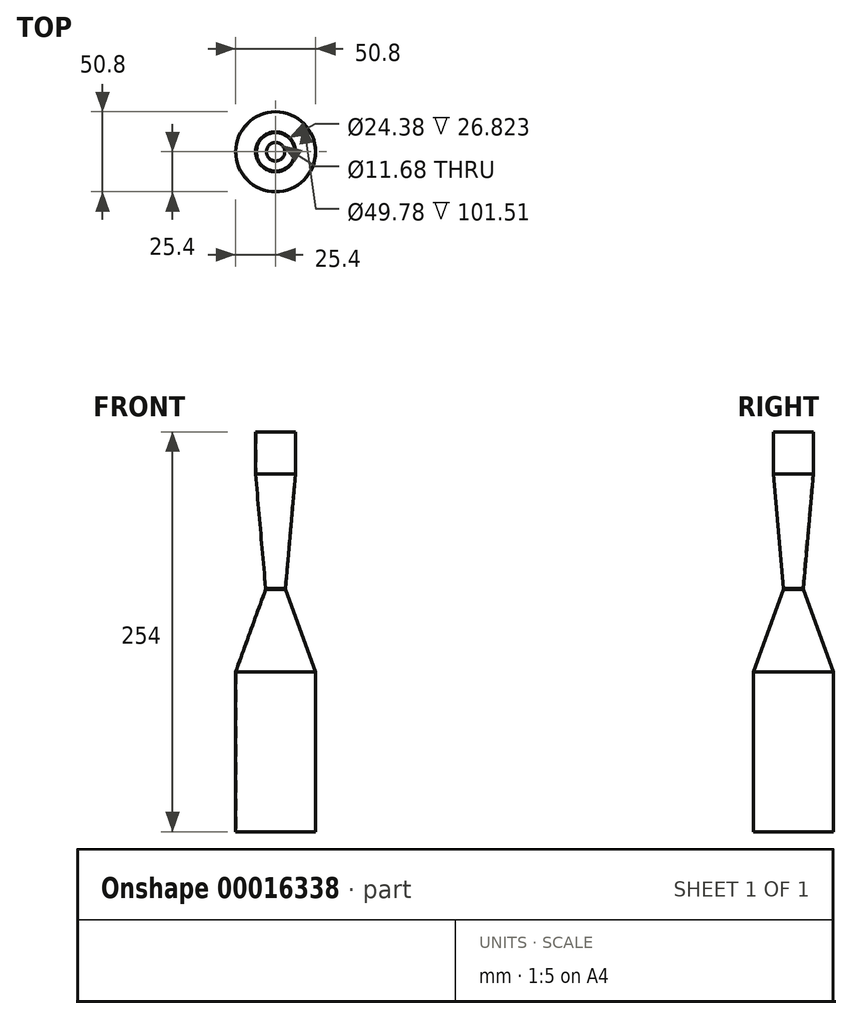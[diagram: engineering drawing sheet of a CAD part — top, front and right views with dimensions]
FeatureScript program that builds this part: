
annotation { "Feature Type Name" : "Feature", "Feature Type Description" : "" }
export const myFeature = defineFeature(function(context is Context, id is Id, definition is map)
    precondition{}
    {
        {
            var Q0;
            Q0=qCreatedBy(makeId("Front.planeOp"),FACE);
            var sketch = newSketch(context, id + "F0", { "sketchPlane" : qUnion([Q0])});
            skLineSegment(sketch, "E0", {"start": v(0, 0) * mm, "end": v(0, 99.43) * mm});
            skLineSegment(sketch, "E1", {"start": v(0, 99.43) * mm, "end": v(-12.7, 99.43) * mm});
            skLineSegment(sketch, "E2", {"start": v(-12.7, 99.43) * mm, "end": v(-12.7, 72.58) * mm});
            skLineSegment(sketch, "E3", {"start": v(-12.7, 72.58) * mm, "end": v(-6.35, 0) * mm});
            skLineSegment(sketch, "E4", {"start": v(-6.35, 0) * mm, "end": v(-6.35, -0.64) * mm});
            skLineSegment(sketch, "E5", {"start": v(-6.35, -0.63) * mm, "end": v(-25.4, -52.97) * mm});
            skLineSegment(sketch, "E6", {"start": v(-25.4, -52.97) * mm, "end": v(-25.4, -154.57) * mm});
            skLineSegment(sketch, "E7", {"start": v(-25.4, -154.57) * mm, "end": v(0, -154.57) * mm});
            skLineSegment(sketch, "E8", {"start": v(-6.35, 0) * mm, "end": v(0, 0) * mm, "construction": true});
            skLineSegment(sketch, "E9", {"start": v(0, 0) * mm, "end": v(0, -154.57) * mm});
            skSolve(sketch);
        }
        {
            var Q0;
            Q0=makeQuery(id+"F0.imprint","IMPRINT",FACE,{"disambiguationData":[TD([[makeQuery(id+"F0.imprint","IMPRINT",EDGE,{"derivedFrom":sQuery(id+"F0.wireOp",EDGE,"E0")}),1.0]])]});
            var Q1;
            Q1=sQuery(id+"F0.wireOp",EDGE,"E0");
            revolve(context, id + "F1", {"entities" : qUnion([Q0]), "axis" : qUnion([Q1]), "revolveType" : RevolveType.FULL});
        }
        {
            var Q0;
            Q0=makeQuery(id+"F1.opRevolve","SWEPT_FACE",FACE,{"disambiguationData":[OSD([sQuery(id+"F0.wireOp",EDGE,"E7")])]});
            var Q1;
            Q1=makeQuery(id+"F1.opRevolve","SWEPT_FACE",FACE,{"disambiguationData":[OSD([sQuery(id+"F0.wireOp",EDGE,"E1")])]});
            shell(context, id + "F2", {"entities" : qUnion([Q0, Q1]), "thickness" : 0.5 * mm});
        }
    });
